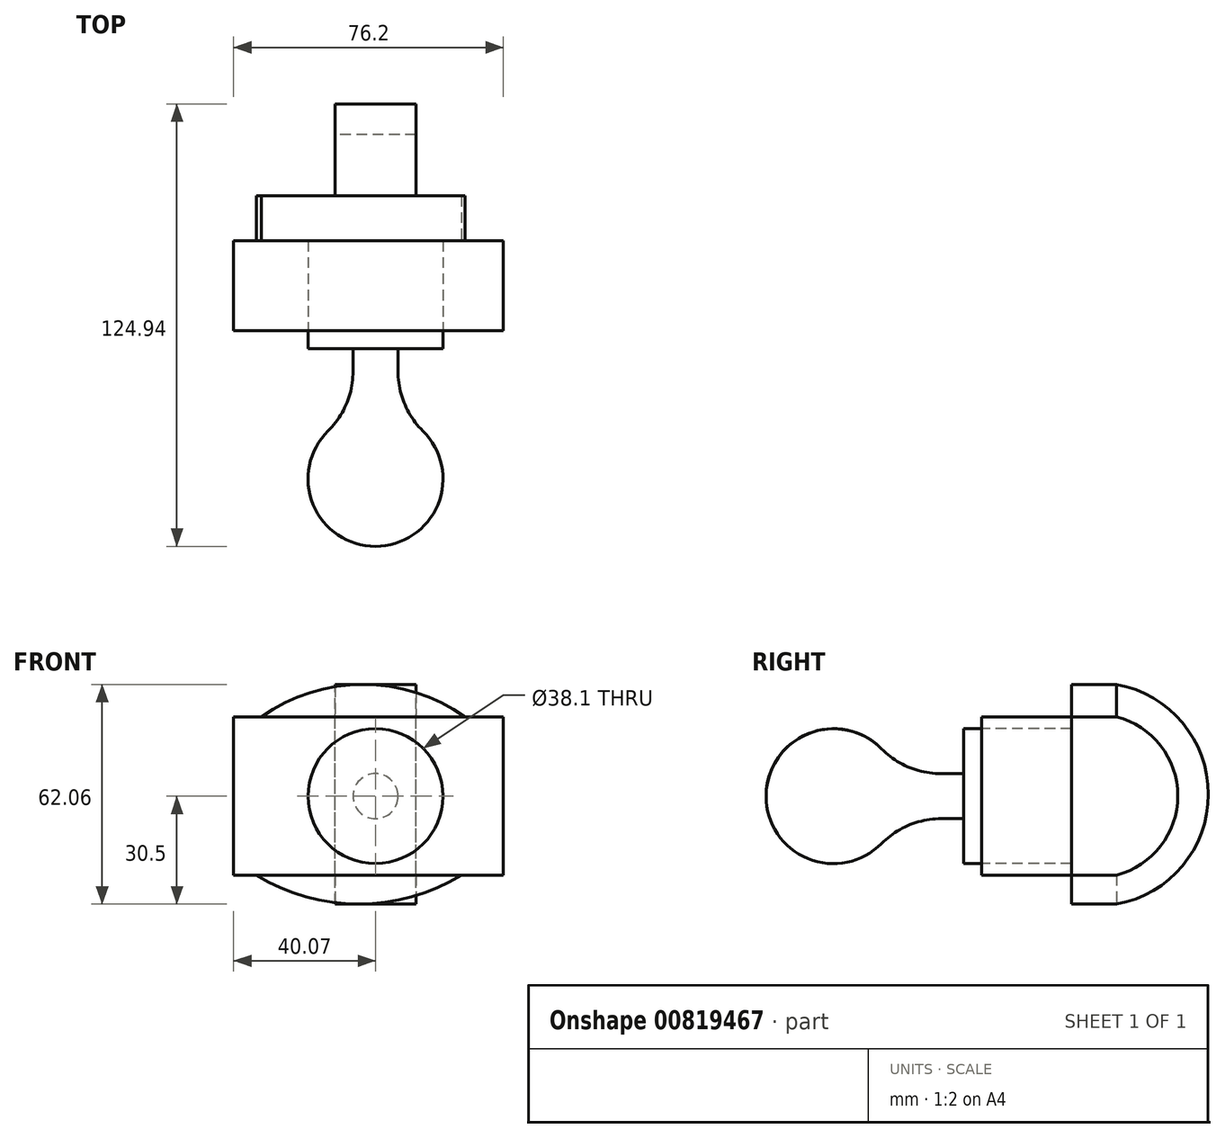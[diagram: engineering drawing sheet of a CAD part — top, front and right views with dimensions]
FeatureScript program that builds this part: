
annotation { "Feature Type Name" : "Feature", "Feature Type Description" : "" }
export const myFeature = defineFeature(function(context is Context, id is Id, definition is map)
    precondition{}
    {
        {
            var Q0;
            Q0=qCreatedBy(makeId("Right.planeOp"),FACE);
            var sketch = newSketch(context, id + "F0", { "sketchPlane" : qUnion([Q0])});
            skArc(sketch, "E0", {"start": v(19.05, 0) * mm, "mid": v(0, 19.05) * mm, "end": v(-19.05, 0) * mm});
            skLineSegment(sketch, "E1.bottom", {"start": v(36.75, 19.05) * mm, "end": v(41.83, 19.05) * mm});
            skLineSegment(sketch, "E1.left", {"start": v(36.75, 19.05) * mm, "end": v(36.75, 0) * mm});
            skLineSegment(sketch, "E1.right", {"start": v(41.83, 19.05) * mm, "end": v(41.83, 0) * mm});
            skLineSegment(sketch, "E2", {"start": v(0, 0) * mm, "end": v(36.75, 0) * mm, "construction": true});
            skArc(sketch, "E3", {"start": v(13.55, 13.4) * mm, "mid": v(21.27, 8.18) * mm, "end": v(30.4, 6.35) * mm});
            skLineSegment(sketch, "E4", {"start": v(30.4, 6.35) * mm, "end": v(36.75, 6.35) * mm});
            skLineSegment(sketch, "E5", {"start": v(-19.05, 0) * mm, "end": v(41.83, 0) * mm});
            skPoint(sketch, "E1.top.end.orphan", {"position": v(41.83, -19.05) * mm});
            skPoint(sketch, "E6.orphan", {"position": v(36.75, -19.05) * mm});
            skSolve(sketch);
        }
        {
            var Q0;
            {var subQ0=sQuery(id+"F0.wireOp",EDGE,"E5");var subQ1=sQuery(id+"F0.wireOp",EDGE,"E0");var subQ2=makeQuery(id+"F0.imprint","INTERSECT",VERTEX,{"disambiguationData":[OD(0.0)],"derivedFrom":[subQ1,subQ0]});Q0=makeQuery(id+"F0.imprint","IMPRINT",FACE,{"disambiguationData":[TD([[makeQuery(id+"F0.imprint","IMPRINT",EDGE,{"disambiguationData":[TD([[subQ2,-1.0]])],"derivedFrom":subQ1}),1.0]])]});}
            var Q1;
            {var subQ1=sQuery(id+"F0.wireOp",EDGE,"E3");Q1=makeQuery(id+"F0.imprint","IMPRINT",FACE,{"disambiguationData":[TD([[makeQuery(id+"F0.imprint","IMPRINT",EDGE,{"derivedFrom":subQ1}),-1.0]])]});}
            var Q2;
            {var subQ5=sQuery(id+"F0.wireOp",EDGE,"E1.bottom");Q2=makeQuery(id+"F0.imprint","IMPRINT",FACE,{"disambiguationData":[TD([[makeQuery(id+"F0.imprint","IMPRINT",EDGE,{"derivedFrom":subQ5}),-1.0]])]});}
            var Q3;
            Q3=sQuery(id+"F0.wireOp",EDGE,"E5");
            revolve(context, id + "F1", {"surfaceOperationType" : NewSurfaceOperationType.NEW, "entities" : qUnion([Q0, Q1, Q2]), "axis" : qUnion([Q3]), "revolveType" : RevolveType.FULL});
        }
        {
            var Q0;
            Q0=makeQuery(id+"F1.opRevolve","SWEPT_FACE",FACE,{"disambiguationData":[OSD([sQuery(id+"F0.wireOp",EDGE,"E1.right")])]});
            var sketch = newSketch(context, id + "F2", { "sketchPlane" : qUnion([Q0])});
            skLineSegment(sketch, "E7.bottom", {"start": v(-36.13, -22.29) * mm, "end": v(40.07, -22.29) * mm});
            skLineSegment(sketch, "E7.top", {"start": v(-36.13, 22.44) * mm, "end": v(40.07, 22.44) * mm});
            skLineSegment(sketch, "E7.left", {"start": v(-36.13, -22.29) * mm, "end": v(-36.13, 22.44) * mm});
            skLineSegment(sketch, "E7.right", {"start": v(40.07, -22.29) * mm, "end": v(40.07, 22.44) * mm});
            skSolve(sketch);
        }
        {
            var Q0;
            Q0=makeQuery(id+"F2.imprint","IMPRINT",FACE,{"disambiguationData":[TD([[makeQuery(id+"F2.imprint","IMPRINT",EDGE,{"derivedFrom":sQuery(id+"F2.wireOp",EDGE,"E7.bottom")}),1.0]])]});
            extrude(context, id + "F3", {"entities" : qUnion([Q0]), "depth" : 25.4 * mm, "offsetDistance" : 25.4 * mm});
        }
        {
            var Q0;
            Q0=makeQuery(id+"F3.opExtrude","CAP_FACE",FACE,{"disambiguationData":[OSD([sQuery(id+"F0.wireOp",EDGE,"E1.bottom"),sQuery(id+"F0.wireOp",EDGE,"E1.right"),sQuery(id+"F2.wireOp",EDGE,"E7.bottom"),sQuery(id+"F2.wireOp",EDGE,"E7.top"),sQuery(id+"F2.wireOp",EDGE,"E7.left"),sQuery(id+"F2.wireOp",EDGE,"E7.right")])],"isStart":false});
            var sketch = newSketch(context, id + "F4", { "sketchPlane" : qUnion([Q0])});
            skArc(sketch, "E8", {"start": v(-24.29, -22.29) * mm, "mid": v(4.7, -30.5) * mm, "end": v(33.69, -22.29) * mm});
            skArc(sketch, "E9", {"start": v(32.3, 22.44) * mm, "mid": v(3.48, 31.56) * mm, "end": v(-25.35, 22.44) * mm});
            skSolve(sketch);
        }
        {
            var Q0;
            {var subQ0=sQuery(id+"F4.wireOp",EDGE,"E8");Q0=makeQuery(id+"F4.imprint","IMPRINT",FACE,{"disambiguationData":[TD([[makeQuery(id+"F4.imprint","IMPRINT",EDGE,{"derivedFrom":subQ0}),1.0]])]});}
            var Q1;
            {var subQ0=sQuery(id+"F4.wireOp",EDGE,"E9");Q1=makeQuery(id+"F4.imprint","IMPRINT",FACE,{"disambiguationData":[TD([[makeQuery(id+"F4.imprint","IMPRINT",EDGE,{"derivedFrom":subQ0}),1.0]])]});}
            extrude(context, id + "F5", {"entities" : qUnion([Q0, Q1]), "depth" : 12.7 * mm, "offsetDistance" : 25.4 * mm});
        }
        {
            var Q0;
            Q0=qCreatedBy(makeId("Right.planeOp"),FACE);
            var sketch = newSketch(context, id + "F6", { "sketchPlane" : qUnion([Q0])});
            skArc(sketch, "E10", {"start": v(79.93, -22.29) * mm, "mid": v(97.25, 0.08) * mm, "end": v(79.93, 22.44) * mm});
            skLineSegment(sketch, "E11", {"start": v(79.93, -30.5) * mm, "end": v(67.23, -30.5) * mm});
            skLineSegment(sketch, "E12", {"start": v(67.23, 31.56) * mm, "end": v(79.93, 31.56) * mm});
            skLineSegment(sketch, "E13.0", {"start": v(79.93, -22.29) * mm, "end": v(67.23, -22.29) * mm});
            skLineSegment(sketch, "E14.0", {"start": v(79.93, 22.44) * mm, "end": v(67.23, 22.44) * mm});
            skArc(sketch, "E15", {"start": v(79.93, -30.5) * mm, "mid": v(105.9, 0.53) * mm, "end": v(79.93, 31.56) * mm});
            skLineSegment(sketch, "E16", {"start": v(79.93, -22.29) * mm, "end": v(79.93, -30.5) * mm});
            skLineSegment(sketch, "E17", {"start": v(79.93, 31.56) * mm, "end": v(79.93, 22.44) * mm});
            skSolve(sketch);
        }
        {
            var Q0;
            Q0=makeQuery(id+"F6.imprint","IMPRINT",FACE,{"disambiguationData":[TD([[makeQuery(id+"F6.imprint","IMPRINT",EDGE,{"derivedFrom":sQuery(id+"F6.wireOp",EDGE,"E10")}),-1.0]])]});
            extrude(context, id + "F7", {"entities" : qUnion([Q0]), "endBound" : BoundingType.SYMMETRIC, "depth" : 22.86 * mm, "offsetDistance" : 25.4 * mm});
        }
    });
